# Revit family: Basin-Counter_Mounted-American_Standard-Cadet-0427_Series
name_source: partatom
category: Plumbing Fixtures
revit_build: Autodesk Revit 2014 (Build: 20130308_1515(x64)
units: mm (PartAtom-declared; Revit-internal decimal feet)

## types (8) — shared parameters
ADA Compliant = Yes
Assembly Code = D2010310
Basin Shape = Round
CW Connection = Yes
CWFU = 1.5
Cold Water Connection Diameter = 3/8"
Cold Water Connection Height = 22 1/2"
Cold Water Connection Radius = 3/16"
Cold Water Connection Width = 4"
Default Elevation = 33 1/4"
HW Connection = Yes
HWFU = 1.5
Height = 8"
Hot Water Connection Diameter = 3/8"
Hot Water Connection Height = 22 1/2"
Hot Water Connection Radius = 3/16"
Hot Water Connection Width = 4"
Installation Type = Counter Mounted
Length = 19"
Manufacturer = American Standard
Price = Prices may vary. Please consult Manufacturer Representative for most up-to-date price list.
Revised Date = 12/11/2018
Vent Connection = No
WFU = 2
Warranty Information = 1 Year Limited
Waste Connection = Yes
Waste Connection Diameter = 1 1/4"
Waste Connection Height = 20 3/8"
Waste Connection Radius = 5/8"
Width = 19"

## per-type parameters (varying)
| type | Description | Finish | Hole Punch Location | Material | Product Documentation Link | Product Page URL | URL |
| 0427.444EC.020 | Cadet Everclean Round Sink with faucet holes on 4" (102mm) centers. | Vitreous China-American Standard-020-White | 4" | Vitreous China-American Standard-020-White | https://www.americanstandard.ca | https://www.americanstandard.ca | https://www.americanstandard.ca |
| 0427.888EC.020 | Cadet Everclean Round Sink with faucet holes on 8" (203mm) centers. | Vitreous China-American Standard-020-White | 8" | Vitreous China-American Standard-020-White | http://www.americanstandard-us.com | http://www.americanstandard-us.com | http://www.americanstandard-us.com |
| 0427.444EC.021 | Cadet Everclean Round Sink with faucet holes on 4" (102mm) centers. | Vitreous China-American Standard-021-Bone | 4" | Vitreous China-American Standard-021-Bone | https://www.americanstandard.ca | https://www.americanstandard.ca | https://www.americanstandard.ca |
| 0427.444EC.178 | Cadet Everclean Round Sink with faucet holes on 4" (102mm) centers. | Vitreous China-American Standard-178-Black | 4" | Vitreous China-American Standard-178-Black | https://www.americanstandard.ca | https://www.americanstandard.ca | https://www.americanstandard.ca |
| 0427.444EC.222 | Cadet Everclean Round Sink with faucet holes on 4" (102mm) centers. | Vitreous China-American Standard-222-Linen | 4" | Vitreous China-American Standard-222-Linen | https://www.americanstandard.ca | https://www.americanstandard.ca | https://www.americanstandard.ca |
| 0427.888EC.021 | Cadet Everclean Round Sink with faucet holes on 8" (203mm) centers. | Vitreous China-American Standard-021-Bone | 8" | Vitreous China-American Standard-021-Bone | http://www.americanstandard-us.com | http://www.americanstandard-us.com | http://www.americanstandard-us.com |
| 0427.888EC.178 | Cadet Everclean Round Sink with faucet holes on 8" (203mm) centers. | Vitreous China-American Standard-178-Black | 8" | Vitreous China-American Standard-178-Black | http://www.americanstandard-us.com | http://www.americanstandard-us.com | http://www.americanstandard-us.com |
| 0427.888EC.222 | Cadet Everclean Round Sink with faucet holes on 8" (203mm) centers. | Vitreous China-American Standard-222-Linen | 8" | Vitreous China-American Standard-222-Linen | http://www.americanstandard-us.com | http://www.americanstandard-us.com | http://www.americanstandard-us.com |

note: column(s) folded — value = type name in every type: Model

## geometry (parser evidence)
native form markers: Sweep x1
no freeform markers — native parametric forms only
